# Revit family: ERA_Оголовок_KIV
name_source: partatom
category: Оборудование
units: mm (PartAtom-declared; Revit-internal decimal feet)

## family parameters
Всегда вертикально = Да
Классификация = Нет
На основе рабочей плоскости = Нет
Общий = Нет
При загрузке вырезать с полостями = Нет
Размер круглого соединителя = Использовать диаметр
Тип детали = Вставляется
Точка расчета площади = Нет

## types (1)
- KIV125
    ADSK_URL документации изделия = https://era.trade
    ADSK_URL страницы изделия = https://era.trade
    ADSK_Версия Revit = 2019
    ADSK_Версия семейства = Ver.1 2025-02
    ADSK_Единица измерения = шт.
    ADSK_Завод-изготовитель = ООО «ЭРА»
    ADSK_Код изделия = KIV125
    ADSK_Количество = 1
    ADSK_Марка = KIV125
    ADSK_Материал = ERA_Условный_Белый
    ADSK_Наименование = Оголовок KIV125
    ADSK_Обозначение = KIV125
    ADSK_Размер_Высота = 190 мм
    ADSK_Размер_Диаметр = 125 мм
    ADSK_Размер_Длина = 146 мм
    ADSK_Размер_Ширина = 190 мм
    Code1 = 1
    ERA_Гарантия = 2 года
    ERA_Количество в транспортной упаковке = 1
    ERA_Контакты = 8 (4912) 70-16-76, 8 (4912) 24-16-00
    ERA_Материал корпуса = пластик
    ERA_Принцип вентиляции = Приточный
    ERA_Размещение = в стену
    ERA_Страна производитель = Россия
    ERA_Температурный диапазон работы = в помещении от +1°С до +40°С и температура перемещаемого воздуха -30°С до +50°С
    ERA_Торговая марка = ERA
    ERA_Управление = Механическое
    ERA_Цвет = Белый
    ERA_Цвет (декоративный) = White
    URL = https://era.trade
    Изготовитель = ООО «ЭРА»
    Производитель_Контакты_Телефон = 8 (4912) 70-16-76, 8 (4912) 24-16-00
